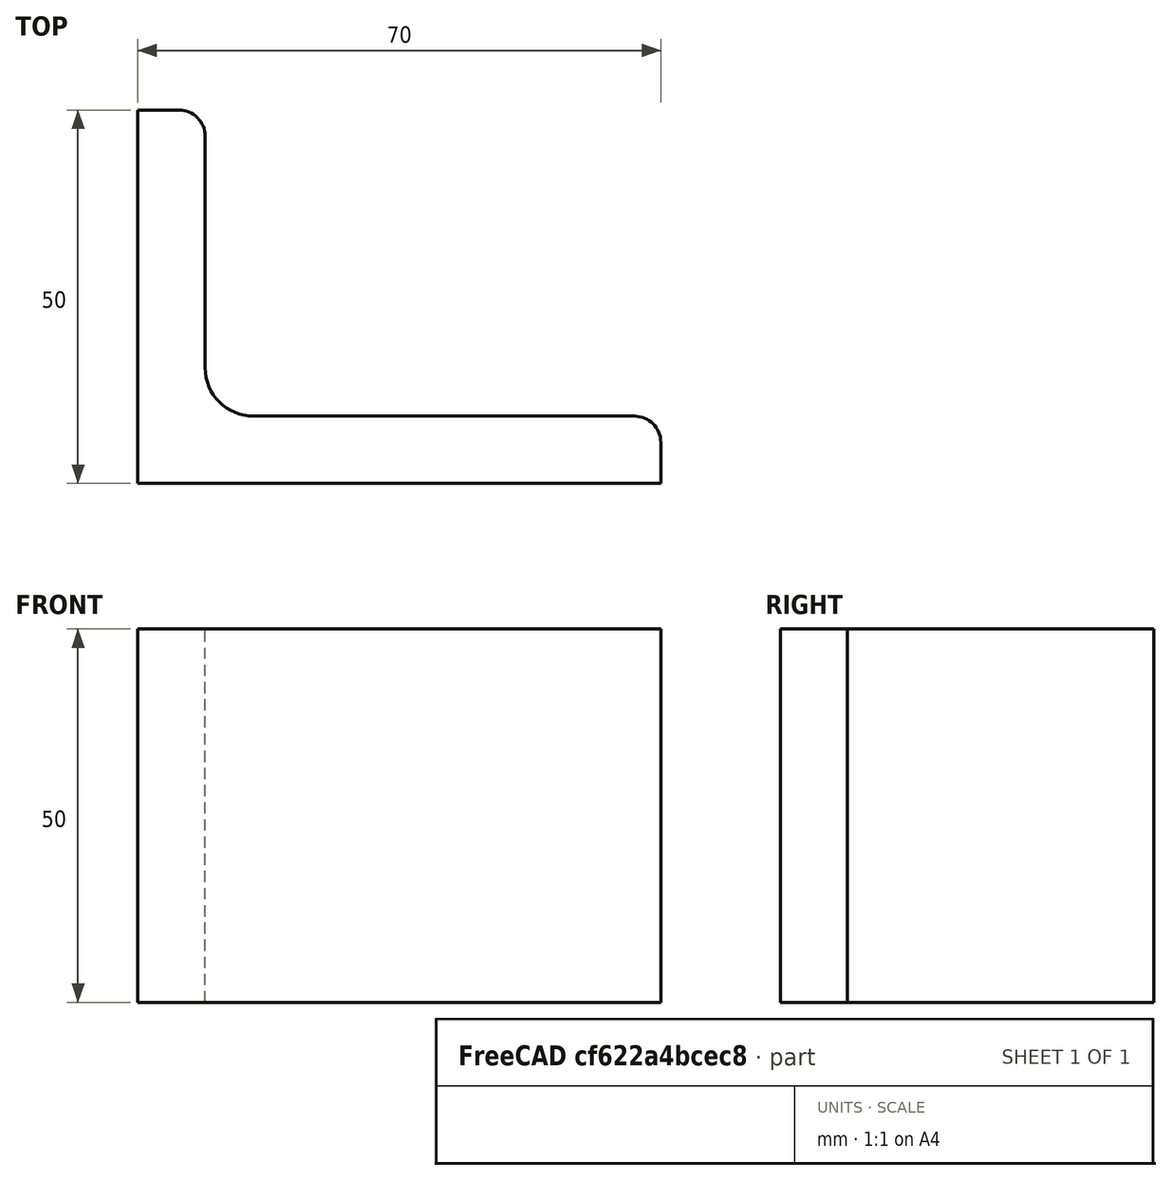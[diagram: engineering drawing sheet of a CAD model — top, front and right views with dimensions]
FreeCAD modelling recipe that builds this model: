
FCSTD DOCUMENT  (FreeCAD 0.15R4671 (Git))
Label: Angle Bar 70x50x9 EN10056 S235JR
License: All rights reserved
LicenseURL: http://en.wikipedia.org/wiki/All_rights_reserved
objects: Sketcher::SketchObject×1, Part::Extrusion×1
note: 2 computed .brp shape members not serialized (recipe doc carries the construction recipe); baked Part::Feature solids carry a one-line shape summary decoded from their .brp

FEATURE [Sketcher::SketchObject] Sketch
  sketch-geometry (9):
    g0: LineSegment StartX=0 StartY=0 StartZ=0 EndX=70 EndY=0 EndZ=0
    g1: LineSegment StartX=70 StartY=0 StartZ=0 EndX=70 EndY=5.5 EndZ=0
    g2: LineSegment StartX=66.5 StartY=9 StartZ=0 EndX=15.5 EndY=9 EndZ=0
    g3: LineSegment StartX=0 StartY=0 StartZ=0 EndX=0 EndY=50 EndZ=0
    g4: LineSegment StartX=0 StartY=50 StartZ=0 EndX=5.5 EndY=50 EndZ=0
    g5: LineSegment StartX=9 StartY=46.5 StartZ=0 EndX=9 EndY=15.5 EndZ=0
    g6: ArcOfCircle CenterX=15.5 CenterY=15.5 CenterZ=0 NormalX=0 NormalY=0 NormalZ=1 Radius=6.5 StartAngle=3.14159 EndAngle=4.71239
    g7: ArcOfCircle CenterX=5.5 CenterY=46.5 CenterZ=0 NormalX=0 NormalY=0 NormalZ=1 Radius=3.5 StartAngle=0 EndAngle=1.5708
    g8: ArcOfCircle CenterX=66.5 CenterY=5.5 CenterZ=0 NormalX=0 NormalY=0 NormalZ=1 Radius=3.5 StartAngle=0 EndAngle=1.5708
  constraints (23):
    c: Coincident(g0,g-1)
    c: Horizontal(g0)
    c: Coincident(g1,g0)
    c: Vertical(g1)
    c: Horizontal(g2)
    c: Coincident(g3,g-1)
    c: Vertical(g3)
    c: Coincident(g4,g3)
    c: Horizontal(g4)
    c: Vertical(g5)
    c: Tangent(g5,g6) = -1.5708
    c: Tangent(g2,g6) = 1.5708
    c: Tangent(g4,g7) = 1.5708
    c: Tangent(g5,g7) = 1.5708
    c: Tangent(g2,g8) = -1.5708
    c: Tangent(g1,g8) = -1.5708
    c: DistanceX(g0) = 70
    c: DistanceY(g3) = 50
    c: DistanceY(g0,g2) = 9
    c: DistanceX(g3,g5) = 9
    c: Radius(g6) = 6.5
    c: Radius(g8) = 3.5
    c: Radius(g7) = 3.5
FEATURE [Part::Extrusion] Extrude  label="Angle Bar 70x50x9 EN10056 S235JR"
  Base = -> Sketch
  Dir = (0,0,50)
  Solid = true
